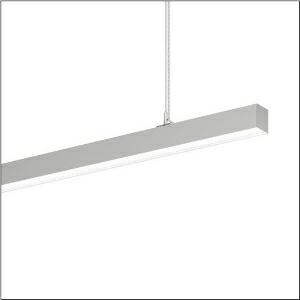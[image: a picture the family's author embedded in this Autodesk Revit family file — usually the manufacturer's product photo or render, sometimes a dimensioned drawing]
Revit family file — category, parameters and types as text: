
# Revit family: silica_r__21_51mx33tbt9s_9dae
name_source: partatom
category: Lighting Fixtures
units: mm (PartAtom-declared; Revit-internal decimal feet)

## family parameters
Cut with Voids When Loaded = No
Host = Face
Light Source = No
Part Type = Normal
Room Calculation Point = No
Round Connector Dimension = Use Diameter
Shared = No

## types (1)
- --- (1 x LED, 7170 lm, 67.4 W, 6500K)
    Apparent Load = 67 VA
    CIE Flux Codes = 78 96 99 56 100
    Color Rendering = 80
    Color Temperature = 6500K
    Default Elevation = 1800 mm
    Description = Silica® 21, office luminaire, primary optical cover: prismatic diffuser, of PMMA, CAT 2 (L<= 3000cd/m²), light emission: direct/indirect distribution, primary light characteristic: symmetric, installation type: suspended mounting, LED, rated luminous flux: 7.170lm, luminous efficacy: 101lm/W, light colour: 8tw, colour temperature: 2700..6500K, control gear: ECG DALI, with terminal, 3+2-pole, max. 2.5mm², mains connection: 220..240V, AC, 50/60Hz, rated input power: 70.8W, luminaire housing, of aluminium, metallic grey (RAL 9006), length: 1.504mm, width: 53mm, height: 53mm, protection rating (complete): IP20, insulation class (complete): insulation class I (protective earthing), certification: CE, permissible operating ambient temperature: 0..+35°C, standard: EN 50419, packaging unit: 1 piece
    Height = 53 mm
    Lamp = 1 x LED
    Lamp Light Flux = 7170 lm
    Lamp Power = 67.4 W
    Lamp count = 1
    Length = 1504 mm
    Luminous efficacy = 106 lm/W
    Manufacturer = Siteco
    ModVariant = No
    Model = 51MX33TBT9S
    Mounting Place = Ceiling
    Mounting Type = Pendant
    Number of Poles = 1
    OnlyDefault = Yes
    Power Factor = 1
    Product Name = Silica® 21
    Product group = office luminaire | ceiling pendant
    ProductGroupID = 905
    Protection Class = Protection class I
    Protection Degree = IP 20
    RLX_Detail_Level = 1
    RlxData = <blob elided: 20173 chars, md5=b57ac238>
    Socket = socket
    Standby Power = 0 W
    System Light Flux = 7170 lm
    System Power = 67 W
    Type Comments = individual setting
    Type Image = l_1251727.jpg
    URL = http://relux.com
    VarID = @adj_045831
    Voltage = 0 V
    Weight = 0.00 kg
    Width = 53 mm

## geometry (parser evidence)
native form markers: Blend x4, Sweep x11
no freeform markers — native parametric forms only
